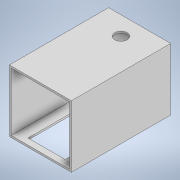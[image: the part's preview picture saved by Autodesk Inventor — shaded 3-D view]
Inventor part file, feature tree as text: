
AUTODESK INVENTOR PART (.ipt)
format: ipt  version: 2020.2 (Build 242310000, 310)  size: 130,048 bytes
history: native  units: mm
features: sketch x4, extrude x3, hole x1
ambient origin geometry x8: Origin, YZ Plane, XZ Plane, XY Plane, X Axis, Y Axis, Z Axis, Center Point
bodies: Solide1 (feature_tree)
feature tree (8):
  extrude  "Extrusion1"  Depth=100.0mm
  extrude  "Extrusion2"  Depth=100.0mm
  hole  "Perçage1"  [1 undecoded]
  extrude  "Extrusion3"  Depth=3.0mm
  sketch  "Esquisse2"
  sketch  "Esquisse3"
  sketch  "Esquisse4"
  sketch  "Esquisse5"
note: 1 required parameter value undecoded (feature->parameter linkage not recoverable at this tier; creation-order binding heuristic only, values carry confidence <= 0.55)
